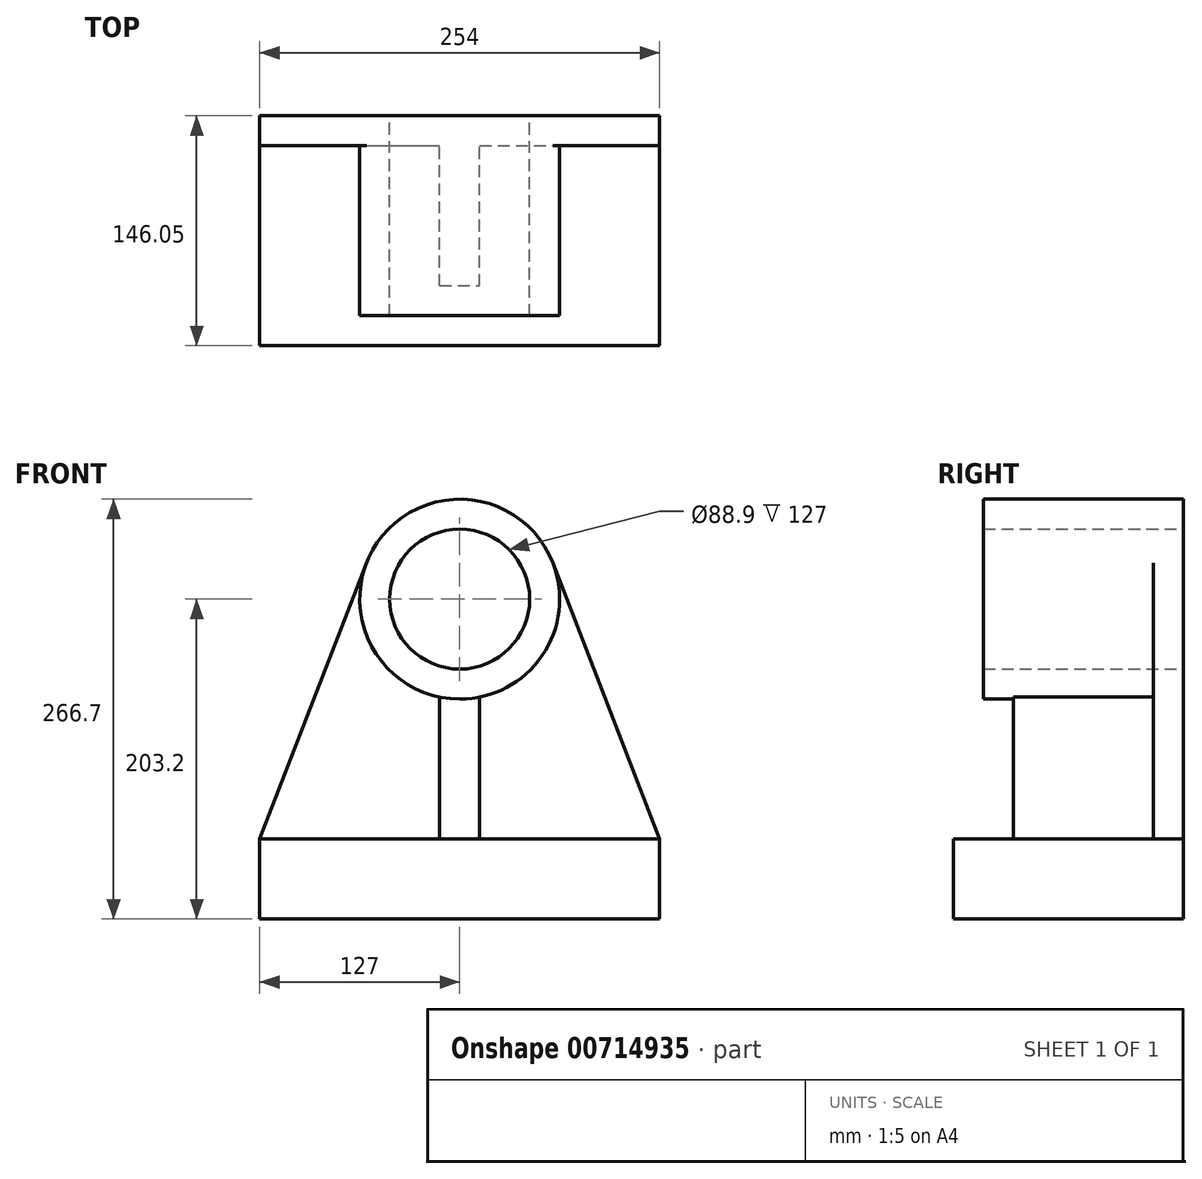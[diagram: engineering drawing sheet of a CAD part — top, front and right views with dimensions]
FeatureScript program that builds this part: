
annotation { "Feature Type Name" : "Feature", "Feature Type Description" : "" }
export const myFeature = defineFeature(function(context is Context, id is Id, definition is map)
    precondition{}
    {
        {
            var Q0;
            Q0=qCreatedBy(makeId("Front.planeOp"),FACE);
            var sketch = newSketch(context, id + "F0", { "sketchPlane" : qUnion([Q0])});
            skArc(sketch, "E0", {"start": v(59.23, 22.9) * mm, "mid": v(0, 63.5) * mm, "end": v(-59.23, 22.9) * mm});
            skLineSegment(sketch, "E1", {"start": v(-59.23, 22.9) * mm, "end": v(-127, -152.4) * mm});
            skLineSegment(sketch, "E2", {"start": v(-127, -152.4) * mm, "end": v(-127, -203.2) * mm});
            skLineSegment(sketch, "E3", {"start": v(-127, -203.2) * mm, "end": v(127, -203.2) * mm});
            skLineSegment(sketch, "E4", {"start": v(127, -203.2) * mm, "end": v(127, -152.4) * mm});
            skLineSegment(sketch, "E5", {"start": v(127, -152.4) * mm, "end": v(59.23, 22.9) * mm});
            skCircle(sketch, "E6", {"center": v(0, 0) * mm, "radius": 44.45 * mm});
            skSolve(sketch);
        }
        {
            var Q0;
            Q0 = qSketchRegion(id + "F0", true);
            extrude(context, id + "F1", {"entities" : qUnion([Q0]), "depth" : 19.05 * mm, "offsetDistance" : 25.4 * mm});
        }
        {
            var Q0;
            Q0=makeQuery(id+"F1.opExtrude","CAP_FACE",FACE,{"disambiguationData":[OSD([sQuery(id+"F0.wireOp",EDGE,"E0"),sQuery(id+"F0.wireOp",EDGE,"E1"),sQuery(id+"F0.wireOp",EDGE,"E2"),sQuery(id+"F0.wireOp",EDGE,"E3"),sQuery(id+"F0.wireOp",EDGE,"E4"),sQuery(id+"F0.wireOp",EDGE,"E5"),sQuery(id+"F0.wireOp",EDGE,"E6")])],"isStart":false});
            var sketch = newSketch(context, id + "F2", { "sketchPlane" : qUnion([Q0])});
            skCircle(sketch, "E7", {"center": v(0, 0) * mm, "radius": 44.45 * mm});
            skCircle(sketch, "E8", {"center": v(0, 0) * mm, "radius": 63.5 * mm});
            skSolve(sketch);
        }
        {
            var Q0;
            Q0 = qSketchRegion(id + "F2", true);
            extrude(context, id + "F3", {"entities" : qUnion([Q0]), "operationType" : NewBodyOperationType.ADD, "depth" : 107.95 * mm, "offsetDistance" : 25.4 * mm});
        }
        {
            var Q0;
            Q0=makeQuery(id+"F1.opExtrude","CAP_FACE",FACE,{"disambiguationData":[OSD([sQuery(id+"F0.wireOp",EDGE,"E0"),sQuery(id+"F0.wireOp",EDGE,"E1"),sQuery(id+"F0.wireOp",EDGE,"E2"),sQuery(id+"F0.wireOp",EDGE,"E3"),sQuery(id+"F0.wireOp",EDGE,"E4"),sQuery(id+"F0.wireOp",EDGE,"E5"),sQuery(id+"F0.wireOp",EDGE,"E6")])],"isStart":false});
            var sketch = newSketch(context, id + "F4", { "sketchPlane" : qUnion([Q0])});
            skLineSegment(sketch, "E9.bottom", {"start": v(-127, -152.4) * mm, "end": v(127, -152.4) * mm});
            skLineSegment(sketch, "E9.top", {"start": v(-127, -203.2) * mm, "end": v(127, -203.2) * mm});
            skLineSegment(sketch, "E9.left", {"start": v(-127, -152.4) * mm, "end": v(-127, -203.2) * mm});
            skLineSegment(sketch, "E9.right", {"start": v(127, -152.4) * mm, "end": v(127, -203.2) * mm});
            skSolve(sketch);
        }
        {
            var Q0;
            Q0 = qSketchRegion(id + "F4", true);
            extrude(context, id + "F5", {"entities" : qUnion([Q0]), "operationType" : NewBodyOperationType.ADD, "depth" : 127 * mm, "offsetDistance" : 25.4 * mm});
        }
        {
            var Q0;
            Q0=makeQuery(id+"F1.opExtrude","CAP_FACE",FACE,{"disambiguationData":[OSD([sQuery(id+"F0.wireOp",EDGE,"E0"),sQuery(id+"F0.wireOp",EDGE,"E1"),sQuery(id+"F0.wireOp",EDGE,"E2"),sQuery(id+"F0.wireOp",EDGE,"E3"),sQuery(id+"F0.wireOp",EDGE,"E4"),sQuery(id+"F0.wireOp",EDGE,"E5"),sQuery(id+"F0.wireOp",EDGE,"E6")])],"isStart":false});
            var sketch = newSketch(context, id + "F6", { "sketchPlane" : qUnion([Q0])});
            skLineSegment(sketch, "E10.bottom", {"start": v(12.7, -152.4) * mm, "end": v(-12.7, -152.4) * mm});
            skLineSegment(sketch, "E10.top", {"start": v(12.7, -53.34) * mm, "end": v(-12.7, -53.34) * mm});
            skLineSegment(sketch, "E10.left", {"start": v(12.7, -152.4) * mm, "end": v(12.7, -53.34) * mm});
            skLineSegment(sketch, "E10.right", {"start": v(-12.7, -152.4) * mm, "end": v(-12.7, -53.34) * mm});
            skPoint(sketch, "E10.middle", {"position": v(0, -102.87) * mm});
            skSolve(sketch);
        }
        {
            var Q0;
            Q0 = qSketchRegion(id + "F6", true);
            extrude(context, id + "F7", {"entities" : qUnion([Q0]), "operationType" : NewBodyOperationType.ADD, "depth" : 88.9 * mm, "offsetDistance" : 25.4 * mm});
        }
    });
